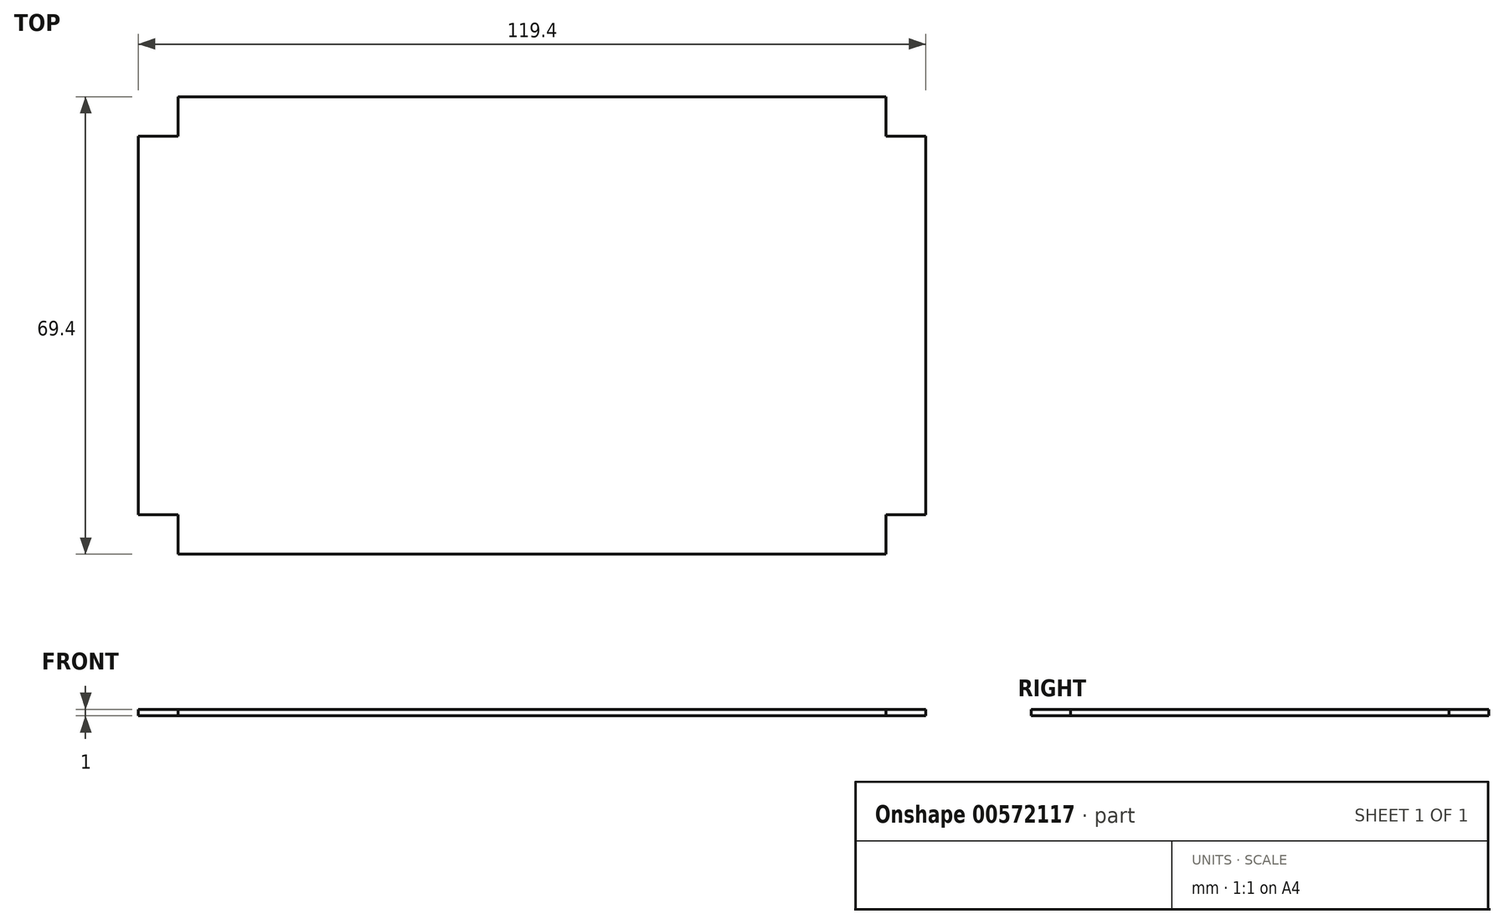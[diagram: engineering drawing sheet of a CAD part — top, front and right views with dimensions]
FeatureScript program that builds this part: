
annotation { "Feature Type Name" : "Feature", "Feature Type Description" : "" }
export const myFeature = defineFeature(function(context is Context, id is Id, definition is map)
    precondition{}
    {
        {
            var Q0;
            Q0=qCreatedBy(makeId("Top.planeOp"),FACE);
            var sketch = newSketch(context, id + "F0", { "sketchPlane" : qUnion([Q0])});
            skPoint(sketch, "E0.middle", {"position": v(0, 0) * mm});
            skLineSegment(sketch, "E1.bottom", {"start": v(-60, 35) * mm, "end": v(60, 35) * mm, "construction": true});
            skLineSegment(sketch, "E1.top", {"start": v(-60, -35) * mm, "end": v(60, -35) * mm, "construction": true});
            skLineSegment(sketch, "E1.left", {"start": v(-60, 35) * mm, "end": v(-60, -35) * mm, "construction": true});
            skLineSegment(sketch, "E1.right", {"start": v(60, 35) * mm, "end": v(60, -35) * mm, "construction": true});
            skLineSegment(sketch, "E2.bottom", {"start": v(-60, 29) * mm, "end": v(-54, 29) * mm, "construction": true});
            skLineSegment(sketch, "E2.right", {"start": v(-54, 29) * mm, "end": v(-54, 35) * mm, "construction": true});
            skLineSegment(sketch, "E3.bottom", {"start": v(-60, -29) * mm, "end": v(-54, -29) * mm, "construction": true});
            skLineSegment(sketch, "E3.top", {"start": v(-60, -35) * mm, "end": v(-54, -35) * mm, "construction": true});
            skLineSegment(sketch, "E3.left", {"start": v(-60, -29) * mm, "end": v(-60, -35) * mm, "construction": true});
            skLineSegment(sketch, "E3.right", {"start": v(-54, -29) * mm, "end": v(-54, -35) * mm, "construction": true});
            skLineSegment(sketch, "E4.bottom", {"start": v(54, 35) * mm, "end": v(60, 35) * mm, "construction": true});
            skLineSegment(sketch, "E4.top", {"start": v(54, 29) * mm, "end": v(60, 29) * mm, "construction": true});
            skLineSegment(sketch, "E4.left", {"start": v(54, 35) * mm, "end": v(54, 29) * mm, "construction": true});
            skLineSegment(sketch, "E4.right", {"start": v(60, 35) * mm, "end": v(60, 29) * mm, "construction": true});
            skLineSegment(sketch, "E5.bottom", {"start": v(60, -29) * mm, "end": v(54, -29) * mm, "construction": true});
            skLineSegment(sketch, "E5.top", {"start": v(60, -35) * mm, "end": v(54, -35) * mm, "construction": true});
            skLineSegment(sketch, "E5.left", {"start": v(60, -29) * mm, "end": v(60, -35) * mm, "construction": true});
            skLineSegment(sketch, "E5.right", {"start": v(54, -29) * mm, "end": v(54, -35) * mm, "construction": true});
            skLineSegment(sketch, "E6.bottom", {"start": v(-59.7, 34.7) * mm, "end": v(59.7, 34.7) * mm});
            skLineSegment(sketch, "E6.top", {"start": v(-59.7, -34.7) * mm, "end": v(59.7, -34.7) * mm});
            skLineSegment(sketch, "E6.left", {"start": v(-59.7, 34.7) * mm, "end": v(-59.7, -34.7) * mm});
            skLineSegment(sketch, "E6.right", {"start": v(59.7, 34.7) * mm, "end": v(59.7, -34.7) * mm});
            skLineSegment(sketch, "E7", {"start": v(-53.7, -34.7) * mm, "end": v(-53.7, -28.7) * mm});
            skLineSegment(sketch, "E8", {"start": v(-53.7, -28.7) * mm, "end": v(-59.7, -28.7) * mm});
            skLineSegment(sketch, "E9", {"start": v(-53.7, 34.7) * mm, "end": v(-53.7, 28.7) * mm});
            skLineSegment(sketch, "E10", {"start": v(-59.7, 28.7) * mm, "end": v(-53.7, 28.7) * mm});
            skLineSegment(sketch, "E11", {"start": v(53.7, 34.7) * mm, "end": v(53.7, 28.7) * mm});
            skLineSegment(sketch, "E12", {"start": v(53.7, 28.7) * mm, "end": v(59.7, 28.7) * mm});
            skLineSegment(sketch, "E13", {"start": v(53.7, -34.7) * mm, "end": v(53.7, -28.7) * mm});
            skLineSegment(sketch, "E14", {"start": v(53.7, -28.7) * mm, "end": v(59.7, -28.7) * mm});
            skSolve(sketch);
        }
        {
            var Q0;
            {var subQ4=sQuery(id+"F0.wireOp",EDGE,"E7");Q0=makeQuery(id+"F0.imprint","IMPRINT",FACE,{"disambiguationData":[TD([[makeQuery(id+"F0.imprint","IMPRINT",EDGE,{"derivedFrom":subQ4}),-1.0]])]});}
            extrude(context, id + "F1", {"entities" : qUnion([Q0]), "depth" : 1 * mm, "offsetDistance" : 25 * mm});
        }
    });
